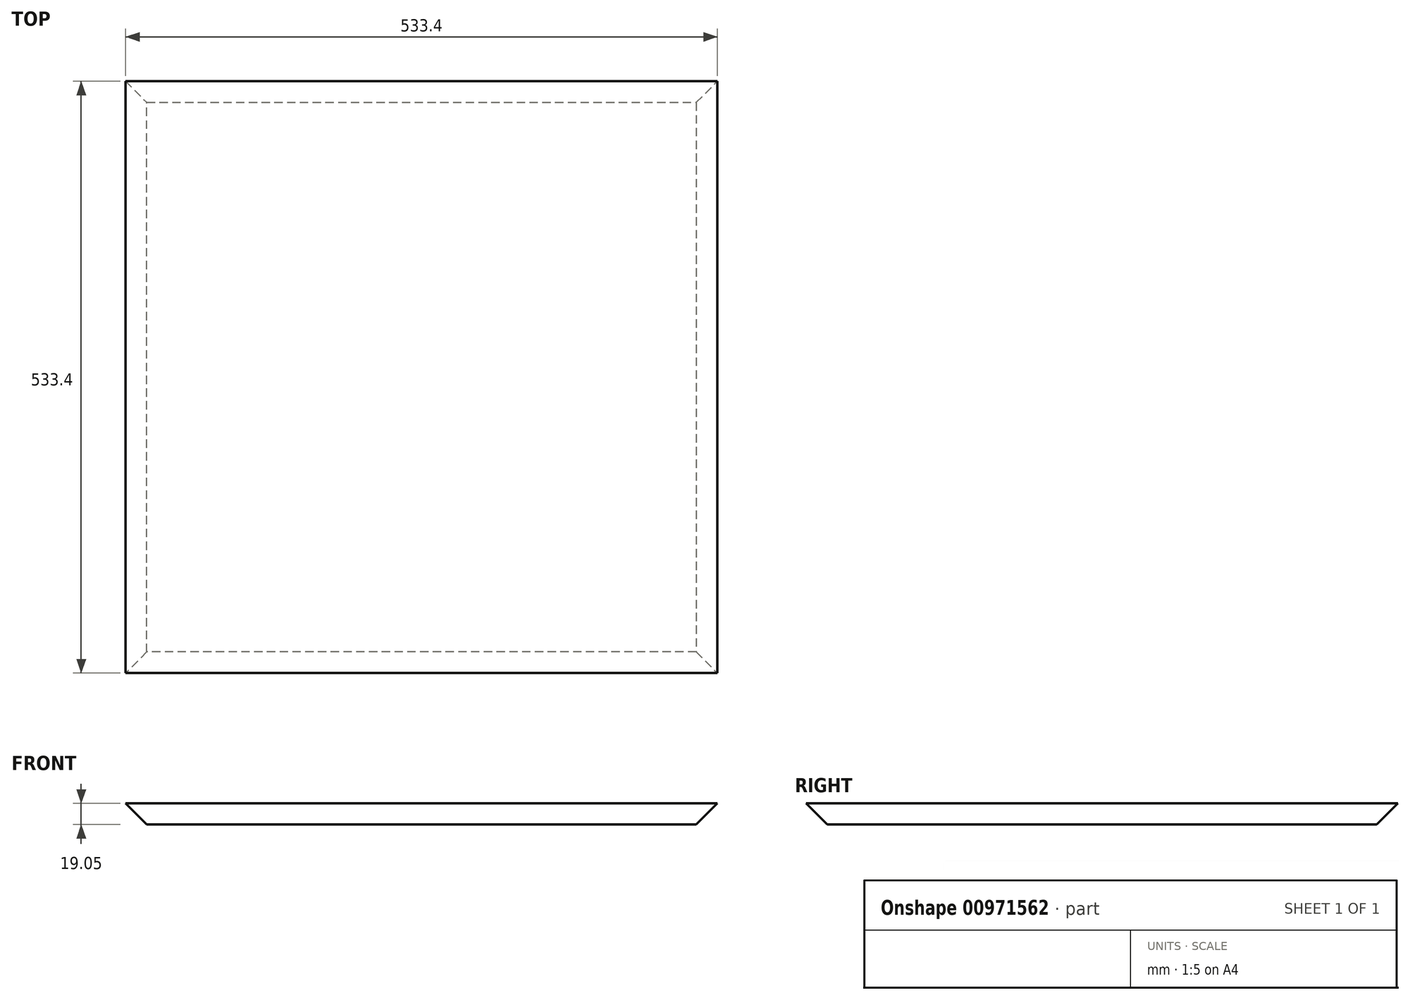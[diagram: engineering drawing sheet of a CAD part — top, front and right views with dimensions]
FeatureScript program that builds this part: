
annotation { "Feature Type Name" : "Feature", "Feature Type Description" : "" }
export const myFeature = defineFeature(function(context is Context, id is Id, definition is map)
    precondition{}
    {
        {
            var Q0;
            Q0=qCreatedBy(makeId("Top.planeOp"),FACE);
            var sketch = newSketch(context, id + "F0", { "sketchPlane" : qUnion([Q0])});
            skLineSegment(sketch, "E0.bottom", {"start": v(-258.43, 314.6) * mm, "end": v(274.97, 314.6) * mm});
            skLineSegment(sketch, "E0.top", {"start": v(-258.43, -218.8) * mm, "end": v(274.97, -218.8) * mm});
            skLineSegment(sketch, "E0.left", {"start": v(-258.43, 314.6) * mm, "end": v(-258.43, -218.8) * mm});
            skLineSegment(sketch, "E0.right", {"start": v(274.97, 314.6) * mm, "end": v(274.97, -218.8) * mm});
            skSolve(sketch);
        }
        {
            var Q0;
            Q0=makeQuery(id+"F0.imprint","IMPRINT",FACE,{"disambiguationData":[TD([[makeQuery(id+"F0.imprint","IMPRINT",EDGE,{"derivedFrom":sQuery(id+"F0.wireOp",EDGE,"E0.bottom")}),-1.0]])]});
            extrude(context, id + "F1", {"entities" : qUnion([Q0]), "depth" : 19.05 * mm, "offsetDistance" : 25.4 * mm});
        }
        {
            var Q0;
            Q0=makeQuery(id+"F1.opExtrude","CAP_EDGE",EDGE,{"disambiguationData":[OSD([sQuery(id+"F0.wireOp",EDGE,"E0.left")])],"isStart":true});
            var Q1;
            Q1=makeQuery(id+"F1.opExtrude","CAP_EDGE",EDGE,{"disambiguationData":[OSD([sQuery(id+"F0.wireOp",EDGE,"E0.top")])],"isStart":true});
            var Q2;
            Q2=makeQuery(id+"F1.opExtrude","CAP_EDGE",EDGE,{"disambiguationData":[OSD([sQuery(id+"F0.wireOp",EDGE,"E0.right")])],"isStart":true});
            var Q3;
            Q3=makeQuery(id+"F1.opExtrude","CAP_EDGE",EDGE,{"disambiguationData":[OSD([sQuery(id+"F0.wireOp",EDGE,"E0.bottom")])],"isStart":true});
            chamfer(context, id + "F2", {"entities" : qUnion([Q0, Q1, Q2, Q3]), "width" : 19.05 * mm, "tangentPropagation" : true});
        }
    });
